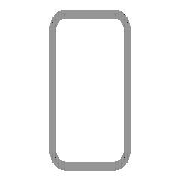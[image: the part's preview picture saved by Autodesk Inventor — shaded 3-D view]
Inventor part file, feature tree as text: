
AUTODESK INVENTOR PART (.ipt)
format: ipt  version: 2025 (Build 290162010, 162A)  size: 129,024 bytes
history: native  units: mm (DEFAULTED — no unit token found)
features: other x3, sketch x1, plane x1
ambient origin geometry x8: Origin, YZ Plane, XZ Plane, XY Plane, X Axis, Y Axis, Z Axis, Center Point
bodies: Solid1 (feature_tree), Body (feature_tree)
feature tree (5):
  other  "Driven Length"
  other  "Start plane"
  other  "End plane"
  sketch  "Sketch3"  dims[d3=1000.0mm d4=0.0mm d7=4.0mm d9=20.0mm d11=40.0mm d12=2.0mm d13=-0.0mm d14=1000.0mm d15=10.0mm d16=20.0mm d17=90.0deg d18=1000.0mm]
  plane  "Work Plane3"
